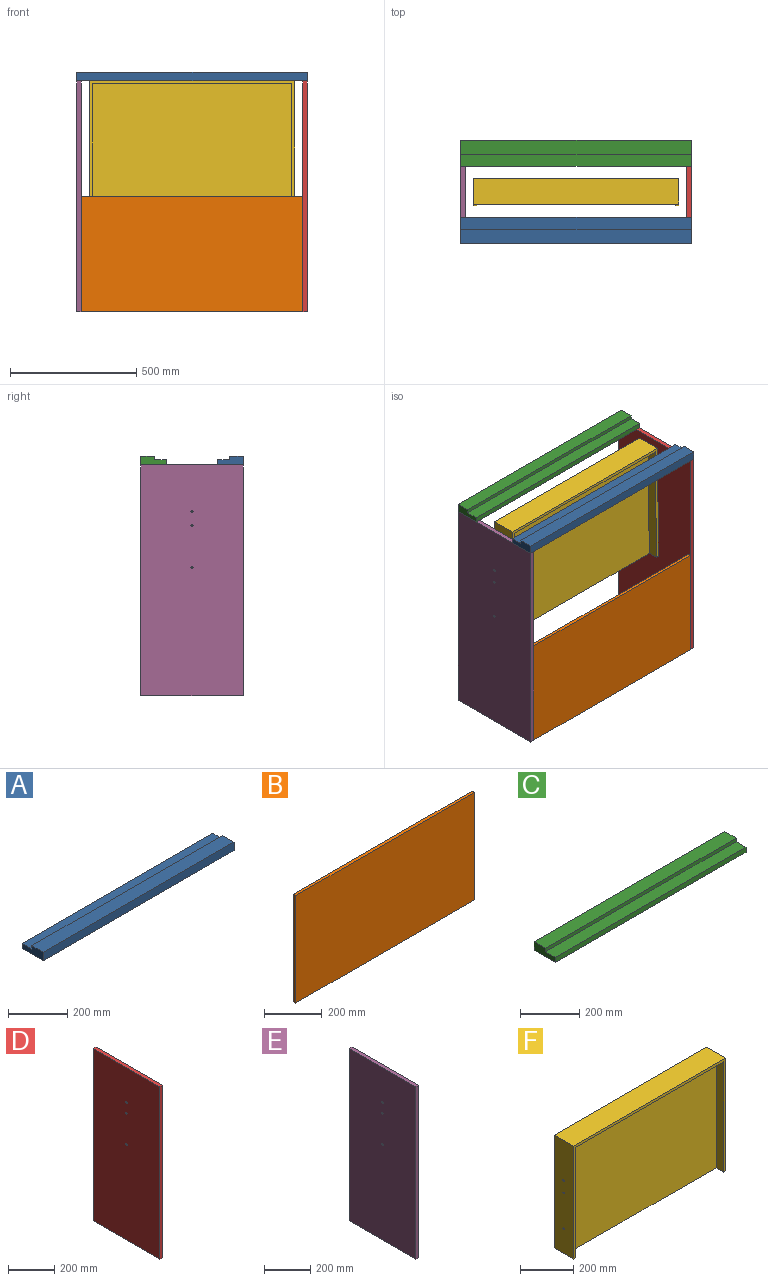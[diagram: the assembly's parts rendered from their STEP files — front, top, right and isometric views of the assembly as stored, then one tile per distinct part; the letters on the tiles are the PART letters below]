
ASSEMBLY  parts=6 mates=5
PART A: 8 faces, bbox 914.4x101.6x35.3 mm
  f0: plane 101.6x35.29mm, normal (1,0,0), area 2903.8mm2, adj f1,f2,f3,f4,f5,f6
  f1: plane 914.4x20.85mm, normal (0,1,0), area 19064.7mm2, adj f0,f2,f6,f7
  f2: plane 914.4x101.6mm, normal (0,0,-1), area 92903mm2, adj f0,f1,f3,f7
  f3: plane 914.4x35.29mm, normal (0,-1,0), area 32273.5mm2, adj f0,f2,f4,f7
  f4: plane 914.4x54.38mm, normal (0,0,1), area 49725.1mm2, adj f0,f3,f5,f7
  f5: plane 914.4x14.45mm, normal (0,1,0), area 13208.8mm2, adj f0,f4,f6,f7
  f6: plane 914.4x47.22mm, normal (0,0,1), area 43177.9mm2, adj f0,f1,f5,f7
  f7: plane 101.6x35.29mm, normal (-1,0,0), area 2903.8mm2, adj f1,f2,f3,f4,f5,f6
PART B: 6 faces, bbox 878.4x12x457.2 mm
  f0: plane 457.2x12mm, normal (-1,0,0), area 5486.4mm2, adj f1,f3,f4,f5
  f1: plane 878.4x12mm, normal (0,0,-1), area 10540.8mm2, adj f0,f2,f3,f4
  f2: plane 457.2x12mm, normal (1,0,0), area 5486.4mm2, adj f1,f3,f4,f5
  f3: plane 878.4x457.2mm, normal (0,-1,0), area 401604.5mm2, adj f0,f1,f2,f5
  f4: plane 878.4x457.2mm, normal (0,1,0), area 401604.5mm2, adj f0,f1,f2,f5
  f5: plane 878.4x12mm, normal (0,0,1), area 10540.8mm2, adj f0,f2,f3,f4
PART C: 8 faces, bbox 914.4x101.6x35.3 mm
  f0: plane 101.6x35.29mm, normal (1,0,0), area 2903.8mm2, adj f1,f2,f3,f5,f6,f7
  f1: plane 914.4x20.85mm, normal (0,-1,0), area 19064.7mm2, adj f0,f2,f4,f5
  f2: plane 914.4x47.22mm, normal (0,0,1), area 43177.9mm2, adj f0,f1,f3,f4
  f3: plane 914.4x14.45mm, normal (0,-1,0), area 13208.8mm2, adj f0,f2,f4,f6
  f4: plane 101.6x35.29mm, normal (-1,0,0), area 2903.8mm2, adj f1,f2,f3,f5,f6,f7
  f5: plane 914.4x101.6mm, normal (0,0,-1), area 92903mm2, adj f0,f1,f4,f7
  f6: plane 914.4x54.38mm, normal (0,0,1), area 49725.1mm2, adj f0,f3,f4,f7
  f7: plane 914.4x35.29mm, normal (0,1,0), area 32273.5mm2, adj f0,f4,f5,f6
PART D: 9 faces, bbox 18x406.4x914.4 mm
  f0: plane 406.4x18mm, normal (0,0,1), area 7315.2mm2, adj f1,f3,f4,f5
  f1: plane 914.4x18mm, normal (0,-1,0), area 16459.2mm2, adj f0,f2,f4,f5
  f2: plane 406.4x18mm, normal (0,0,-1), area 7315.2mm2, adj f1,f3,f4,f5
  f3: plane 914.4x18mm, normal (0,1,0), area 16459.2mm2, adj f0,f2,f4,f5
  f4: plane 914.4x406.4mm, normal (-1,0,0), area 371463.7mm2, adj f0,f1,f2,f3,f6,f7,f8
  f5: plane 914.4x406.4mm, normal (1,0,0), area 371463.7mm2, adj f0,f1,f2,f3,f6,f7,f8
  f6: cylinder r=3.97mm len=18mm, axis (1,0,0), area 448.9mm2, adj f4,f5
  f7: cylinder r=3.97mm len=18mm, axis (1,0,0), area 448.9mm2, adj f4,f5
  f8: cylinder r=3.97mm len=18mm, axis (1,0,0), area 448.9mm2, adj f4,f5
PART E: 9 faces, bbox 18x406.4x914.4 mm
  f0: plane 406.4x18mm, normal (0,0,1), area 7315.2mm2, adj f1,f3,f4,f5
  f1: plane 914.4x18mm, normal (0,-1,0), area 16459.2mm2, adj f0,f2,f4,f5
  f2: plane 406.4x18mm, normal (0,0,-1), area 7315.2mm2, adj f1,f3,f4,f5
  f3: plane 914.4x18mm, normal (0,1,0), area 16459.2mm2, adj f0,f2,f4,f5
  f4: plane 914.4x406.4mm, normal (1,0,0), area 371463.7mm2, adj f0,f1,f2,f3,f6,f7,f8
  f5: plane 914.4x406.4mm, normal (-1,0,0), area 371463.7mm2, adj f0,f1,f2,f3,f6,f7,f8
  f6: cylinder r=3.97mm len=18mm, axis (1,0,0), area 448.9mm2, adj f4,f5
  f7: cylinder r=3.97mm len=18mm, axis (1,0,0), area 448.9mm2, adj f4,f5
  f8: cylinder r=3.97mm len=18mm, axis (1,0,0), area 448.9mm2, adj f4,f5
PART F: 26 faces, bbox 812.8x101.6x520 mm
  f0: plane 788.8x40.22mm, normal (0,0,-1), area 31728.6mm2, adj f3,f10,f11,f12
  f1: plane 812.8x520mm, normal (0,1,0), area 21945.6mm2, adj f2,f4,f5,f6,f7,f9,f13
  f2: plane 520x101.6mm, normal (-1,0,0), area 52683.6mm2, adj f1,f3,f5,f13,f20,f22,f24
  f3: plane 812.8x520mm, normal (0,-1,0), area 21945.6mm2, adj f0,f2,f4,f5,f10,f12,f13
  f4: plane 520x101.6mm, normal (1,0,0), area 52683.6mm2, adj f1,f3,f5,f13,f14,f16,f18
  f5: plane 812.8x101.6mm, normal (0,0,1), area 82580.5mm2, adj f1,f2,f3,f4
  f6: plane 788.8x49.38mm, normal (0,0,-1), area 38947.8mm2, adj f1,f7,f8,f9
  f7: plane 508x49.38mm, normal (1,0,0), area 25083mm2, adj f1,f6,f8,f13
  f8: plane 788.8x508mm, normal (0,1,0), area 400710.4mm2, adj f6,f7,f9,f13
  f9: plane 508x49.38mm, normal (-1,0,0), area 25083mm2, adj f1,f6,f8,f13
  f10: plane 508x40.22mm, normal (-1,0,0), area 20433.8mm2, adj f0,f3,f11,f13
  f11: plane 788.8x508mm, normal (0,-1,0), area 400710.4mm2, adj f0,f10,f12,f13
  f12: plane 508x40.22mm, normal (1,0,0), area 20433.8mm2, adj f0,f3,f11,f13
  f13: plane 812.8x101.6mm, normal (0,0,-1), area 11904mm2, adj f1,f2,f3,f4,f7,f8,f9,f10
  f14: cylinder r=3.97mm len=9.53mm, axis (1,0,0), area 237.5mm2, adj f4,f15
  f15: plane 7.94x7.94mm, normal (1,0,0), area 49.5mm2, adj f14
  f16: cylinder r=3.97mm len=9.53mm, axis (1,0,0), area 237.5mm2, adj f4,f17
  f17: plane 7.94x7.94mm, normal (1,0,0), area 49.5mm2, adj f16
  f18: cylinder r=3.97mm len=9.53mm, axis (1,0,0), area 237.5mm2, adj f4,f19
  f19: plane 7.94x7.94mm, normal (1,0,0), area 49.5mm2, adj f18
  f20: cylinder r=3.97mm len=9.53mm, axis (-1,0,0), area 237.5mm2, adj f2,f21
  f21: plane 7.94x7.94mm, normal (-1,0,0), area 49.5mm2, adj f20
  f22: cylinder r=3.97mm len=9.53mm, axis (-1,0,0), area 237.5mm2, adj f2,f23
  f23: plane 7.94x7.94mm, normal (-1,0,0), area 49.5mm2, adj f22
  f24: cylinder r=3.97mm len=9.53mm, axis (-1,0,0), area 237.5mm2, adj f2,f25
  f25: plane 7.94x7.94mm, normal (-1,0,0), area 49.5mm2, adj f24
PLACE A t=(-914.4,0,0)mm
PLACE B t=(-914.4,0,0)mm
PLACE C t=(-914.4,0,0)mm
PLACE D t=(-914.4,0,0)mm
PLACE E t=(-914.4,0,0)mm
PLACE F rot(axis=(-1,0,0),0.7deg) t=(-862.55,154.5,903.01)mm
MATE fastened E.f0 <-> A.f2  axis (0,0,1) through (-914.4,0,914.4)mm
MATE fastened C.f5 <-> E.f0  axis (0,0,-1) through (-914.4,406.4,914.4)mm
MATE fastened A.f2 <-> D.f0  axis (0,0,-1) through (0,0,914.4)mm
MATE revolute F.f18 <-> D.f8  axis (1,0,0) through (-49.75,203.2,730.25)mm
MATE fastened B.f0 <-> E.f4  axis (-1,0,0) through (-896.4,0,0)mm
